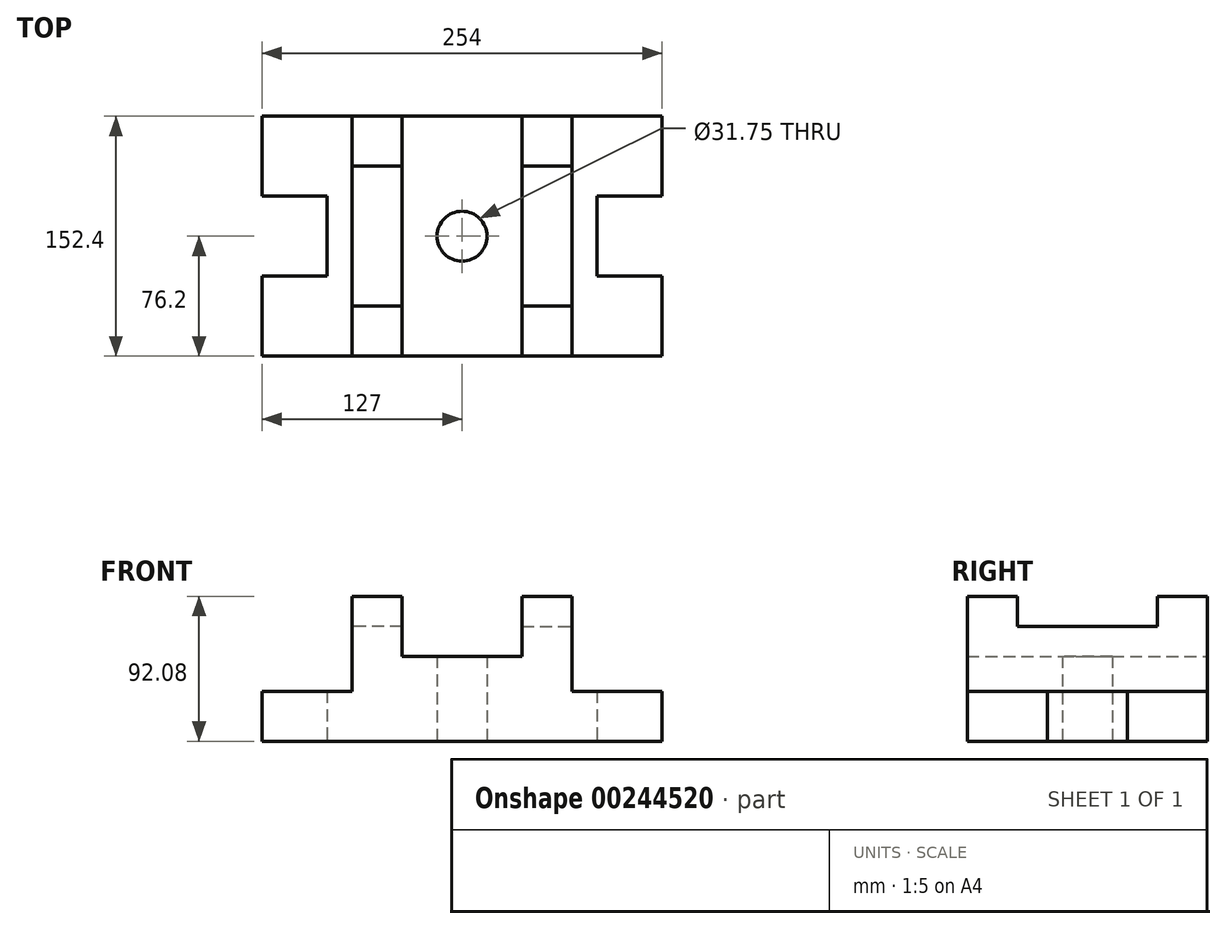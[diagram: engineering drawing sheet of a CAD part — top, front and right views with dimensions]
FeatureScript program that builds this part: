
annotation { "Feature Type Name" : "Feature", "Feature Type Description" : "" }
export const myFeature = defineFeature(function(context is Context, id is Id, definition is map)
    precondition{}
    {
        {
            var Q0;
            Q0=qCreatedBy(makeId("Top.planeOp"),FACE);
            var sketch = newSketch(context, id + "F0", { "sketchPlane" : qUnion([Q0])});
            skArc(sketch, "E0", {"start": v(0, -15.88) * mm, "mid": v(15.88, 0) * mm, "end": v(0, 15.88) * mm});
            skLineSegment(sketch, "E1", {"start": v(0, 15.88) * mm, "end": v(0, -15.88) * mm});
            skLineSegment(sketch, "E2", {"start": v(0, 76.2) * mm, "end": v(38.1, 76.2) * mm});
            skLineSegment(sketch, "E3.bottom", {"start": v(38.1, 76.2) * mm, "end": v(69.85, 76.2) * mm});
            skLineSegment(sketch, "E3.top", {"start": v(38.1, 44.45) * mm, "end": v(69.85, 44.45) * mm});
            skLineSegment(sketch, "E3.left", {"start": v(38.1, 76.2) * mm, "end": v(38.1, 44.45) * mm});
            skLineSegment(sketch, "E3.right", {"start": v(69.85, 76.2) * mm, "end": v(69.85, 44.45) * mm});
            skPoint(sketch, "E4.orphan", {"position": v(-127, 0) * mm});
            skPoint(sketch, "E5.end.orphan", {"position": v(-38.1, 76.2) * mm});
            skLineSegment(sketch, "E6", {"start": v(0, -76.2) * mm, "end": v(38.1, -76.2) * mm});
            skLineSegment(sketch, "E7.bottom", {"start": v(38.1, -76.2) * mm, "end": v(69.85, -76.2) * mm});
            skLineSegment(sketch, "E7.top", {"start": v(38.1, -44.45) * mm, "end": v(69.85, -44.45) * mm});
            skLineSegment(sketch, "E7.left", {"start": v(38.1, -76.2) * mm, "end": v(38.1, -44.45) * mm});
            skLineSegment(sketch, "E7.right", {"start": v(69.85, -76.2) * mm, "end": v(69.85, -44.45) * mm});
            skLineSegment(sketch, "E8", {"start": v(38.1, 44.45) * mm, "end": v(38.1, -44.45) * mm});
            skLineSegment(sketch, "E9", {"start": v(69.85, 44.45) * mm, "end": v(69.85, -44.45) * mm});
            skLineSegment(sketch, "E10", {"start": v(69.85, -76.2) * mm, "end": v(127, -76.2) * mm});
            skPoint(sketch, "E10.endSnap0", {"position": v(53.98, -76.2) * mm});
            skLineSegment(sketch, "E11", {"start": v(69.85, 76.2) * mm, "end": v(127, 76.2) * mm});
            skLineSegment(sketch, "E12", {"start": v(127, -76.2) * mm, "end": v(127, -25.4) * mm});
            skLineSegment(sketch, "E13", {"start": v(127, 76.2) * mm, "end": v(127, 25.4) * mm});
            skLineSegment(sketch, "E14.bottom", {"start": v(127, -25.4) * mm, "end": v(85.73, -25.4) * mm});
            skLineSegment(sketch, "E14.top", {"start": v(127, 25.4) * mm, "end": v(85.73, 25.4) * mm});
            skLineSegment(sketch, "E14.right", {"start": v(85.73, -25.4) * mm, "end": v(85.73, 25.4) * mm});
            skLineSegment(sketch, "E15.MirrorCS", {"start": v(-85.73, -25.4) * mm, "end": v(-85.73, 25.4) * mm});
            skLineSegment(sketch, "E16.MirrorCS", {"start": v(-38.1, 44.45) * mm, "end": v(-38.1, -44.45) * mm});
            skLineSegment(sketch, "E17.MirrorCS", {"start": v(-69.85, -76.2) * mm, "end": v(-69.85, -44.45) * mm});
            skLineSegment(sketch, "E18.MirrorCS", {"start": v(-38.1, -76.2) * mm, "end": v(-38.1, -44.45) * mm});
            skLineSegment(sketch, "E19.MirrorCS", {"start": v(-38.1, -44.45) * mm, "end": v(-69.85, -44.45) * mm});
            skLineSegment(sketch, "E20.MirrorCS", {"start": v(-38.1, -76.2) * mm, "end": v(-69.85, -76.2) * mm});
            skLineSegment(sketch, "E21.MirrorCS", {"start": v(0, -76.2) * mm, "end": v(-38.1, -76.2) * mm});
            skLineSegment(sketch, "E22.MirrorCS", {"start": v(-38.1, 76.2) * mm, "end": v(-69.85, 76.2) * mm});
            skLineSegment(sketch, "E23.MirrorCS", {"start": v(-38.1, 44.45) * mm, "end": v(-69.85, 44.45) * mm});
            skLineSegment(sketch, "E24.MirrorCS", {"start": v(-38.1, 76.2) * mm, "end": v(-38.1, 44.45) * mm});
            skLineSegment(sketch, "E25.MirrorCS", {"start": v(-127, -25.4) * mm, "end": v(-85.73, -25.4) * mm});
            skLineSegment(sketch, "E26.MirrorCS", {"start": v(0, 76.2) * mm, "end": v(-38.1, 76.2) * mm});
            skArc(sketch, "E27.MirrorCS", {"start": v(0, -15.88) * mm, "mid": v(-15.88, 0) * mm, "end": v(0, 15.88) * mm});
            skLineSegment(sketch, "E28.MirrorCS", {"start": v(-69.85, 76.2) * mm, "end": v(-69.85, 44.45) * mm});
            skLineSegment(sketch, "E29.MirrorCS", {"start": v(-127, -76.2) * mm, "end": v(-127, -25.4) * mm});
            skLineSegment(sketch, "E30.MirrorCS", {"start": v(-69.85, 44.45) * mm, "end": v(-69.85, -44.45) * mm});
            skLineSegment(sketch, "E31.MirrorCS", {"start": v(-127, 25.4) * mm, "end": v(-85.73, 25.4) * mm});
            skPoint(sketch, "E32.MirrorP", {"position": v(-53.98, -76.2) * mm});
            skLineSegment(sketch, "E33.MirrorCS", {"start": v(-69.85, -76.2) * mm, "end": v(-127, -76.2) * mm});
            skLineSegment(sketch, "E34.MirrorCS", {"start": v(-127, 76.2) * mm, "end": v(-127, 25.4) * mm});
            skLineSegment(sketch, "E35.MirrorCS", {"start": v(-69.85, 76.2) * mm, "end": v(-127, 76.2) * mm});
            skSolve(sketch);
        }
        {
            var Q0;
            Q0=makeQuery(id+"F0.imprint","IMPRINT",FACE,{"disambiguationData":[TD([[makeQuery(id+"F0.imprint","IMPRINT",EDGE,{"derivedFrom":sQuery(id+"F0.wireOp",EDGE,"E15.MirrorCS")}),-1.0]])]});
            var Q1;
            Q1=makeQuery(id+"F0.imprint","IMPRINT",FACE,{"disambiguationData":[TD([[makeQuery(id+"F0.imprint","IMPRINT",EDGE,{"derivedFrom":sQuery(id+"F0.wireOp",EDGE,"E3.right")}),1.0]])]});
            extrude(context, id + "F1", {"entities" : qUnion([Q0, Q1]), "depth" : 31.75 * mm});
        }
        {
            var Q0;
            Q0=makeQuery(id+"F0.imprint","IMPRINT",FACE,{"disambiguationData":[TD([[makeQuery(id+"F0.imprint","IMPRINT",EDGE,{"derivedFrom":sQuery(id+"F0.wireOp",EDGE,"E22.MirrorCS")}),1.0]])]});
            var Q1;
            Q1=makeQuery(id+"F0.imprint","IMPRINT",FACE,{"disambiguationData":[TD([[makeQuery(id+"F0.imprint","IMPRINT",EDGE,{"derivedFrom":sQuery(id+"F0.wireOp",EDGE,"E17.MirrorCS")}),-1.0]])]});
            var Q2;
            Q2=makeQuery(id+"F0.imprint","IMPRINT",FACE,{"disambiguationData":[TD([[makeQuery(id+"F0.imprint","IMPRINT",EDGE,{"derivedFrom":sQuery(id+"F0.wireOp",EDGE,"E7.bottom")}),1.0]])]});
            var Q3;
            Q3=makeQuery(id+"F0.imprint","IMPRINT",FACE,{"disambiguationData":[TD([[makeQuery(id+"F0.imprint","IMPRINT",EDGE,{"derivedFrom":sQuery(id+"F0.wireOp",EDGE,"E3.bottom")}),-1.0]])]});
            extrude(context, id + "F2", {"entities" : qUnion([Q0, Q1, Q2, Q3]), "operationType" : NewBodyOperationType.ADD, "depth" : 92.07 * mm});
        }
        {
            var Q0;
            Q0=makeQuery(id+"F0.imprint","IMPRINT",FACE,{"disambiguationData":[TD([[makeQuery(id+"F0.imprint","IMPRINT",EDGE,{"derivedFrom":sQuery(id+"F0.wireOp",EDGE,"E0")}),-1.0]])]});
            extrude(context, id + "F3", {"entities" : qUnion([Q0]), "operationType" : NewBodyOperationType.ADD, "depth" : 53.97 * mm});
        }
        {
            var Q0;
            Q0=makeQuery(id+"F0.imprint","IMPRINT",FACE,{"disambiguationData":[TD([[makeQuery(id+"F0.imprint","IMPRINT",EDGE,{"derivedFrom":sQuery(id+"F0.wireOp",EDGE,"E16.MirrorCS")}),-1.0]])]});
            var Q1;
            Q1=makeQuery(id+"F0.imprint","IMPRINT",FACE,{"disambiguationData":[TD([[makeQuery(id+"F0.imprint","IMPRINT",EDGE,{"derivedFrom":sQuery(id+"F0.wireOp",EDGE,"E3.top")}),-1.0]])]});
            extrude(context, id + "F4", {"entities" : qUnion([Q0, Q1]), "operationType" : NewBodyOperationType.ADD, "depth" : 73.02 * mm});
        }
    });
